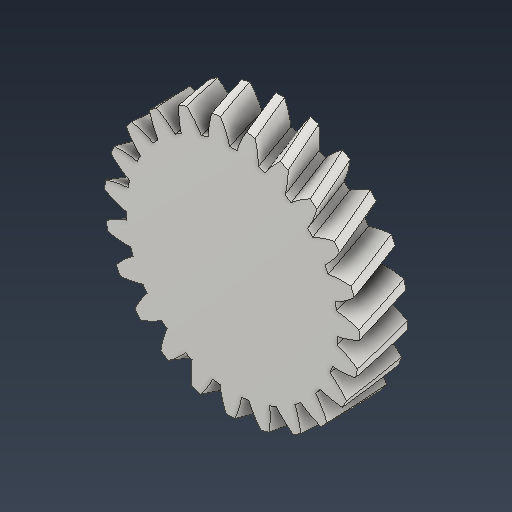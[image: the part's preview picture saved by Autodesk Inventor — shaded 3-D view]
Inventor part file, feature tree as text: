
AUTODESK INVENTOR PART (.ipt)
format: ipt  version: 2022 (Build 260153000, 153)  size: 494,592 bytes
history: native  units: mm (DEFAULTED — no unit token found)
features: plane x3, other x3, sketch x2, extrude x1
ambient origin geometry x8: Origin, YZ Plane, XZ Plane, XY Plane, X Axis, Y Axis, Z Axis, Center Point
bodies: Solid1 (feature_tree)
feature tree (9):
  extrude  "Extrusion1"  Depth=10.0mm TaperAngle=0.0deg
  plane  "Work Plane2"
  plane  "Work Plane8"
  plane  "Work Plane9"
  other  "Spur Gear"
  sketch  "Sketch1"  dims[d0=52.952178mm d1=10.0mm d2=0.0mm]
  sketch  "Sketch2"  dims[d3=48.952178mm d4=10.0mm d5=0.0mm d16=104.0mm d17=0.0mm d34=1.36591mm d39=0.0mm d41=0.0mm d43=104.0mm d46=104.0mm d47=0.0mm d48=0.0mm]
  other  "Srf1"
  other  "Pitch Diameter"
